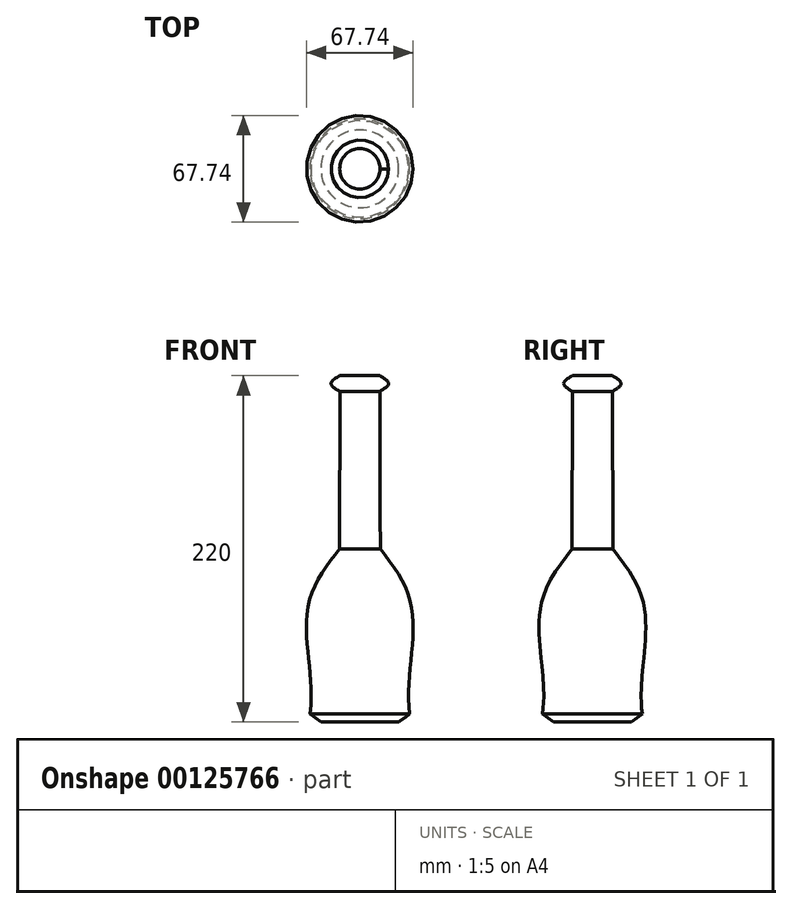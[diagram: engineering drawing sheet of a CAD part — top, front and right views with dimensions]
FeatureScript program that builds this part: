
annotation { "Feature Type Name" : "Feature", "Feature Type Description" : "" }
export const myFeature = defineFeature(function(context is Context, id is Id, definition is map)
    precondition{}
    {
        {
            var Q0;
            Q0=qCreatedBy(makeId("Top.planeOp"),FACE);
            cPlane(context, id + "F0", {"entities" : qUnion([Q0]), "cplaneType" : CPlaneType.OFFSET, "offset" : 40 * mm, "width" : 152.4 * mm, "height" : 152.4 * mm});
        }
        {
            var Q0;
            Q0=qCreatedBy(makeId("Top.planeOp"),FACE);
            cPlane(context, id + "F1", {"entities" : qUnion([Q0]), "cplaneType" : CPlaneType.OFFSET, "offset" : 40 * mm, "oppositeDirection" : true, "width" : 150 * mm, "height" : 150 * mm});
        }
        {
            var Q0;
            Q0=qCreatedBy(id+"F1.planeOp",FACE);
            cPlane(context, id + "F2", {"entities" : qUnion([Q0]), "cplaneType" : CPlaneType.OFFSET, "offset" : 5 * mm, "width" : 150 * mm, "height" : 150 * mm});
        }
        {
            var Q0;
            Q0=qCreatedBy(id+"F1.planeOp",FACE);
            var sketch = newSketch(context, id + "F3", { "sketchPlane" : qUnion([Q0])});
            skCircle(sketch, "E0", {"center": v(0, 0) * mm, "radius": 24.66 * mm});
            skSolve(sketch);
        }
        {
            var Q0;
            Q0=qCreatedBy(id+"F2.planeOp",FACE);
            var sketch = newSketch(context, id + "F4", { "sketchPlane" : qUnion([Q0])});
            skCircle(sketch, "E1", {"center": v(0, 0) * mm, "radius": 31.65 * mm});
            skSolve(sketch);
        }
        {
            var Q0;
            Q0=qCreatedBy(id+"F0.planeOp",FACE);
            var sketch = newSketch(context, id + "F5", { "sketchPlane" : qUnion([Q0])});
            skCircle(sketch, "E2", {"center": v(0, 0) * mm, "radius": 31.16 * mm});
            skSolve(sketch);
        }
        {
            var Q0;
            Q0=qCreatedBy(id+"F0.planeOp",FACE);
            cPlane(context, id + "F6", {"entities" : qUnion([Q0]), "cplaneType" : CPlaneType.OFFSET, "offset" : 30 * mm, "width" : 150 * mm, "height" : 150 * mm});
        }
        {
            var Q0;
            Q0=qCreatedBy(id+"F6.planeOp",FACE);
            var sketch = newSketch(context, id + "F7", { "sketchPlane" : qUnion([Q0])});
            skCircle(sketch, "E3", {"center": v(0, 0) * mm, "radius": 13.03 * mm});
            skSolve(sketch);
        }
        {
            var Q0;
            Q0=qCreatedBy(id+"F6.planeOp",FACE);
            cPlane(context, id + "F8", {"entities" : qUnion([Q0]), "cplaneType" : CPlaneType.OFFSET, "offset" : 100 * mm, "width" : 150 * mm, "height" : 150 * mm});
        }
        {
            var Q0;
            Q0=qCreatedBy(id+"F8.planeOp",FACE);
            var sketch = newSketch(context, id + "F9", { "sketchPlane" : qUnion([Q0])});
            skCircle(sketch, "E4", {"center": v(0, 0) * mm, "radius": 12.7 * mm});
            skSolve(sketch);
        }
        {
            var Q0;
            Q0=qCreatedBy(id+"F8.planeOp",FACE);
            cPlane(context, id + "F10", {"entities" : qUnion([Q0]), "cplaneType" : CPlaneType.OFFSET, "offset" : 5 * mm, "width" : 150 * mm, "height" : 150 * mm});
        }
        {
            var Q0;
            Q0=qCreatedBy(id+"F10.planeOp",FACE);
            var sketch = newSketch(context, id + "F11", { "sketchPlane" : qUnion([Q0])});
            skCircle(sketch, "E5", {"center": v(0, 0) * mm, "radius": 18.24 * mm});
            skSolve(sketch);
        }
        {
            var Q0;
            Q0=qCreatedBy(id+"F10.planeOp",FACE);
            cPlane(context, id + "F12", {"entities" : qUnion([Q0]), "cplaneType" : CPlaneType.OFFSET, "offset" : 5 * mm, "width" : 150 * mm, "height" : 150 * mm});
        }
        {
            var Q0;
            Q0=qCreatedBy(id+"F12.planeOp",FACE);
            var sketch = newSketch(context, id + "F13", { "sketchPlane" : qUnion([Q0])});
            skCircle(sketch, "E6", {"center": v(0, 0) * mm, "radius": 12.78 * mm});
            skSolve(sketch);
        }
        {
            var Q0;
            Q0=qCreatedBy(id+"F2.planeOp",FACE);
            cPlane(context, id + "F14", {"entities" : qUnion([Q0]), "cplaneType" : CPlaneType.OFFSET, "offset" : 5 * mm, "width" : 150 * mm, "height" : 150 * mm});
        }
        {
            var Q0;
            Q0=qCreatedBy(id+"F14.planeOp",FACE);
            var sketch = newSketch(context, id + "F15", { "sketchPlane" : qUnion([Q0])});
            skCircle(sketch, "E7", {"center": v(0, 0) * mm, "radius": 31.16 * mm});
            skSolve(sketch);
        }
        {
            var Q0;
            Q0 = qSketchRegion(id + "F3", true);
            var Q1;
            Q1 = qSketchRegion(id + "F4", true);
            loft(context, id + "F16", {"sheetProfilesArray" : [{ "sheetProfileEntities" : qUnion([Q0]) }, { "sheetProfileEntities" : qUnion([Q1]) }]});
        }
        {
            var Q0;
            Q0 = qSketchRegion(id + "F4", true);
            var Q1;
            Q1 = qSketchRegion(id + "F15", true);
            var Q2;
            Q2 = qSketchRegion(id + "F5", true);
            var Q3;
            Q3 = qSketchRegion(id + "F7", true);
            loft(context, id + "F17", {"sheetProfilesArray" : [{ "sheetProfileEntities" : qUnion([Q0]) }, { "sheetProfileEntities" : qUnion([Q1]) }, { "sheetProfileEntities" : qUnion([Q2]) }, { "sheetProfileEntities" : qUnion([Q3]) }]});
        }
        {
            var Q0;
            Q0 = qSketchRegion(id + "F7", true);
            var Q1;
            Q1 = qSketchRegion(id + "F9", true);
            loft(context, id + "F18", {"sheetProfilesArray" : [{ "sheetProfileEntities" : qUnion([Q0]) }, { "sheetProfileEntities" : qUnion([Q1]) }]});
        }
        {
            var Q0;
            Q0 = qSketchRegion(id + "F9", true);
            var Q1;
            Q1 = qSketchRegion(id + "F11", true);
            var Q2;
            Q2 = qSketchRegion(id + "F13", true);
            loft(context, id + "F19", {"sheetProfilesArray" : [{ "sheetProfileEntities" : qUnion([Q0]) }, { "sheetProfileEntities" : qUnion([Q1]) }, { "sheetProfileEntities" : qUnion([Q2]) }]});
        }
    });
